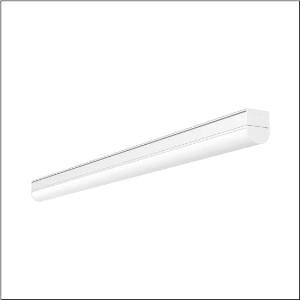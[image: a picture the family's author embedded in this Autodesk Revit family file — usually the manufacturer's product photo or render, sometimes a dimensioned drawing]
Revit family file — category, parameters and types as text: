
# Revit family: ecopack_r__31_51lj12mnm70a_41d1
name_source: partatom
category: Lighting Fixtures
units: mm (PartAtom-declared; Revit-internal decimal feet)

## family parameters
Cut with Voids When Loaded = No
Host = Face
Light Source = No
Part Type = Normal
Room Calculation Point = No
Round Connector Dimension = Use Diameter
Shared = No

## types (1)
- --- (1 x LED, 6780 lm, 50 W, 5000K)
    Apparent Load = 50 VA
    CIE Flux Codes = 39 67 87 89 100
    Color Rendering = 80
    Color Temperature = 5000K
    Default Elevation = 1800 mm
    Description = Ecopack® 31, diffuser luminaire, primary optical cover: cover, of PC, frosted, light emission: direct distribution, primary light characteristic: symmetric, installation type: surface-mounted, LED, rated luminous flux: 7.000lm, luminous efficacy: 140lm/W, light colour: 830/840/850, colour temperature: 3000/4000/5000K, control gear: ECG, with terminal, 3-pole, mains connection: 220..240V, AC, 50/60Hz, rated input power: 50W, housing, of aluminium, traffic white (RAL 9016), length: 1.450mm, width: 56mm, height: 68mm, end cap, of PC, white, protection rating (complete): IP20, insulation class (complete): insulation class I (protective earthing), certification: CE, impact resistance: IK06, permissible operating ambient temperature: -20..+40°C, packaging unit: 1 piece
    Height = 68 mm
    Lamp = 1 x LED
    Lamp Light Flux = 6780 lm
    Lamp Power = 50 W
    Lamp count = 1
    Length = 1450 mm
    Luminous efficacy = 136 lm/W
    Manufacturer = Siteco
    ModVariant = No
    Model = 51LJ12MNM70A
    Mounting Place = Ceiling
    Mounting Type = Surface mounted
    Number of Poles = 1
    OnlyDefault = Yes
    Power Factor = 1
    Product Name = Ecopack® 31
    Product group = diffuser luminaire
    ProductGroupID = 304
    Protection Class = Protection class I
    Protection Degree = IP 20
    RLX_Detail_Level = 1
    RLX_Emergency_Light_Flux = 0 lm
    RLX_Emergency_Type = 0
    RLX_Emergency_Type_DB = No
    RlxData = <blob elided: 38961 chars, md5=28db1089>
    Socket = socket
    Standby Power = 0 W
    System Light Flux = 6780 lm
    System Power = 50 W
    Type Comments = individual setting: colour temperature 5000K, luminous flux: 100 % | (ON | ON)
    Type Image = l_1007033.jpg
    URL = http://relux.com
    VarID = @adj_124901
    Voltage = 0 V
    Weight = 0.00 kg
    Width = 56 mm

## geometry (parser evidence)
native form markers: Blend x4, Sweep x15
no freeform markers — native parametric forms only
